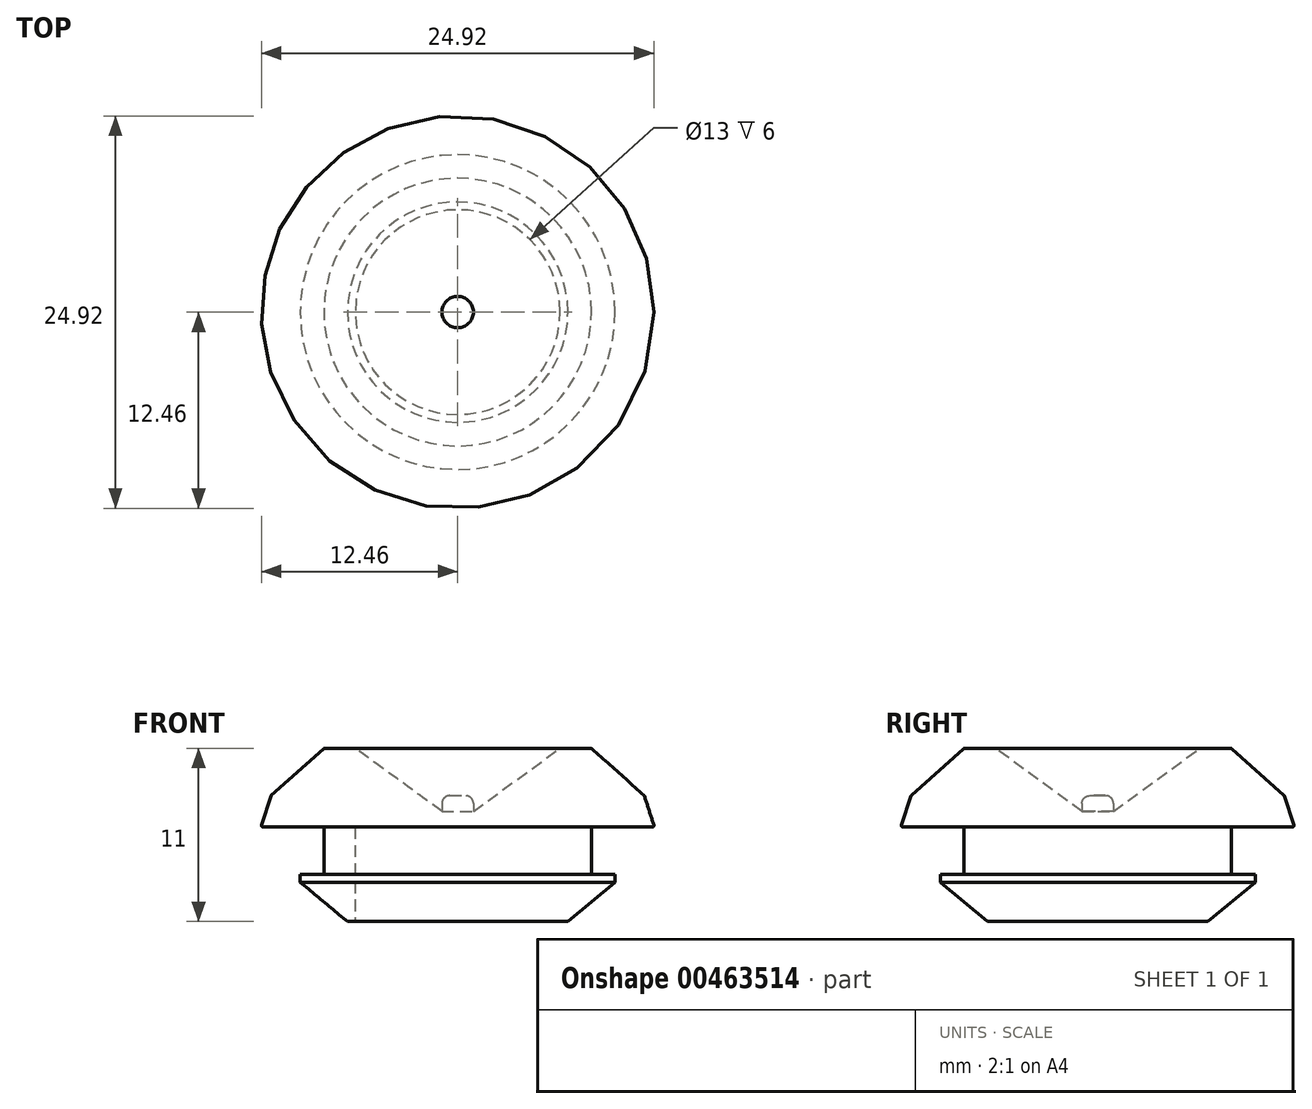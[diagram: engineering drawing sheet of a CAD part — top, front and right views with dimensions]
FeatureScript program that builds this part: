
annotation { "Feature Type Name" : "Feature", "Feature Type Description" : "" }
export const myFeature = defineFeature(function(context is Context, id is Id, definition is map)
    precondition{}
    {
        {
            var Q0;
            Q0=qCreatedBy(makeId("Front.planeOp"),FACE);
            var sketch = newSketch(context, id + "F0", { "sketchPlane" : qUnion([Q0])});
            skLineSegment(sketch, "E0", {"start": v(0, 2) * mm, "end": v(1, 2) * mm});
            skLineSegment(sketch, "E1", {"start": v(1, 2) * mm, "end": v(1, 1) * mm});
            skLineSegment(sketch, "E2", {"start": v(1, 1) * mm, "end": v(6.5, 5) * mm});
            skLineSegment(sketch, "E3", {"start": v(6.5, 5) * mm, "end": v(8.5, 5) * mm});
            skLineSegment(sketch, "E4", {"start": v(8.5, 5) * mm, "end": v(11.85, 2) * mm});
            skLineSegment(sketch, "E5", {"start": v(11.85, 2) * mm, "end": v(12.5, 0) * mm});
            skLineSegment(sketch, "E6", {"start": v(0, 0) * mm, "end": v(0, 2) * mm});
            skLineSegment(sketch, "E7", {"start": v(12.5, 0) * mm, "end": v(8.5, 0) * mm});
            skLineSegment(sketch, "E8", {"start": v(8.5, 0) * mm, "end": v(8.5, -3) * mm});
            skLineSegment(sketch, "E9", {"start": v(8.5, -3) * mm, "end": v(10, -3) * mm});
            skLineSegment(sketch, "E10", {"start": v(10, -3) * mm, "end": v(10, -3.5) * mm});
            skLineSegment(sketch, "E11", {"start": v(10, -3.5) * mm, "end": v(7, -6) * mm});
            skLineSegment(sketch, "E12", {"start": v(7, -6) * mm, "end": v(6.5, -6) * mm});
            skLineSegment(sketch, "E13", {"start": v(6.5, -6) * mm, "end": v(6.5, 0) * mm});
            skLineSegment(sketch, "E14", {"start": v(6.5, 0) * mm, "end": v(0, 0) * mm});
            skSolve(sketch);
        }
        {
            var Q0;
            Q0=makeQuery(id+"F0.imprint","IMPRINT",FACE,{"disambiguationData":[TD([[makeQuery(id+"F0.imprint","IMPRINT",EDGE,{"derivedFrom":sQuery(id+"F0.wireOp",EDGE,"E0")}),-1.0]])]});
            var Q1;
            Q1=sQuery(id+"F0.wireOp",EDGE,"E6");
            revolve(context, id + "F1", {"surfaceOperationType" : NewSurfaceOperationType.NEW, "entities" : qUnion([Q0]), "axis" : qUnion([Q1]), "revolveType" : RevolveType.FULL});
        }
        {
            var Q0;
            Q0=makeQuery(id+"F1.opRevolve","SWEPT_EDGE",EDGE,{"disambiguationData":[OSD([sQuery(id+"F0.wireOp",EDGE,"E0"),sQuery(id+"F0.wireOp",EDGE,"E1")])]});
            fillet(context, id + "F2", {"entities" : qUnion([Q0]), "radius" : 0.5 * mm, "tangentPropagation" : true, "allowEdgeOverflow" : false});
        }
        {
            var Q0;
            Q0=makeQuery(id+"F1.opRevolve","SWEPT_EDGE",EDGE,{"disambiguationData":[OSD([sQuery(id+"F0.wireOp",EDGE,"E2"),sQuery(id+"F0.wireOp",EDGE,"E3")])]});
            var Q1;
            Q1=makeQuery(id+"F1.opRevolve","SWEPT_EDGE",EDGE,{"disambiguationData":[OSD([sQuery(id+"F0.wireOp",EDGE,"E3"),sQuery(id+"F0.wireOp",EDGE,"E4")])]});
            var Q2;
            Q2=makeQuery(id+"F1.opRevolve","SWEPT_EDGE",EDGE,{"disambiguationData":[OSD([sQuery(id+"F0.wireOp",EDGE,"E4"),sQuery(id+"F0.wireOp",EDGE,"E5")])]});
            var Q3;
            Q3=makeQuery(id+"F1.opRevolve","SWEPT_EDGE",EDGE,{"disambiguationData":[OSD([sQuery(id+"F0.wireOp",EDGE,"E5"),sQuery(id+"F0.wireOp",EDGE,"E7")])]});
            fillet(context, id + "F3", {"entities" : qUnion([Q0, Q1, Q2, Q3]), "radius" : .1 * mm, "tangentPropagation" : true, "allowEdgeOverflow" : false});
        }
    });
